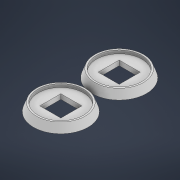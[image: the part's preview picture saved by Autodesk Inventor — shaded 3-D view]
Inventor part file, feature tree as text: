
AUTODESK INVENTOR PART (.ipt)
format: ipt  version: 2022 (Build 260153000, 153)  size: 131,072 bytes
history: native  units: mm
features: extrude x3, sketch x3, thicken_offset x1, draft x1, pattern_linear x1
ambient origin geometry x8: Origin, YZ Plane, XZ Plane, XY Plane, X Axis, Y Axis, Z Axis, Center Point
bodies: Solid1 (feature_tree)
feature tree (9):
  extrude  "Extrusion1"  Depth=15.0mm
  extrude  "Extrusion2"  Depth=6.5mm
  extrude  "Extrusion3"  TaperAngle=0.0deg  [1 undecoded]
  thicken_offset  "Thicken1"
  draft  "FaceDraft1"
  pattern_linear  "Rectangular Pattern1"  Spacing1=14.0mm  [1 undecoded]
  sketch  "Sketch1"  dims[d0=14.0mm d1=15.0mm]
  sketch  "Sketch2"  dims[d2=3.0mm d3=0.0mm d4=6.5mm]
  sketch  "Sketch3"  dims[d5=6.5mm d6=0.0mm d7=0.0mm d8=14.0mm d9=1.0mm d10=0.0mm d11=0.5mm d12=0.5mm d13=3.490659mm d15=20.0mm d17=18.0mm]
note: 2 required parameter values undecoded (feature->parameter linkage not recoverable at this tier; creation-order binding heuristic only, values carry confidence <= 0.55)
